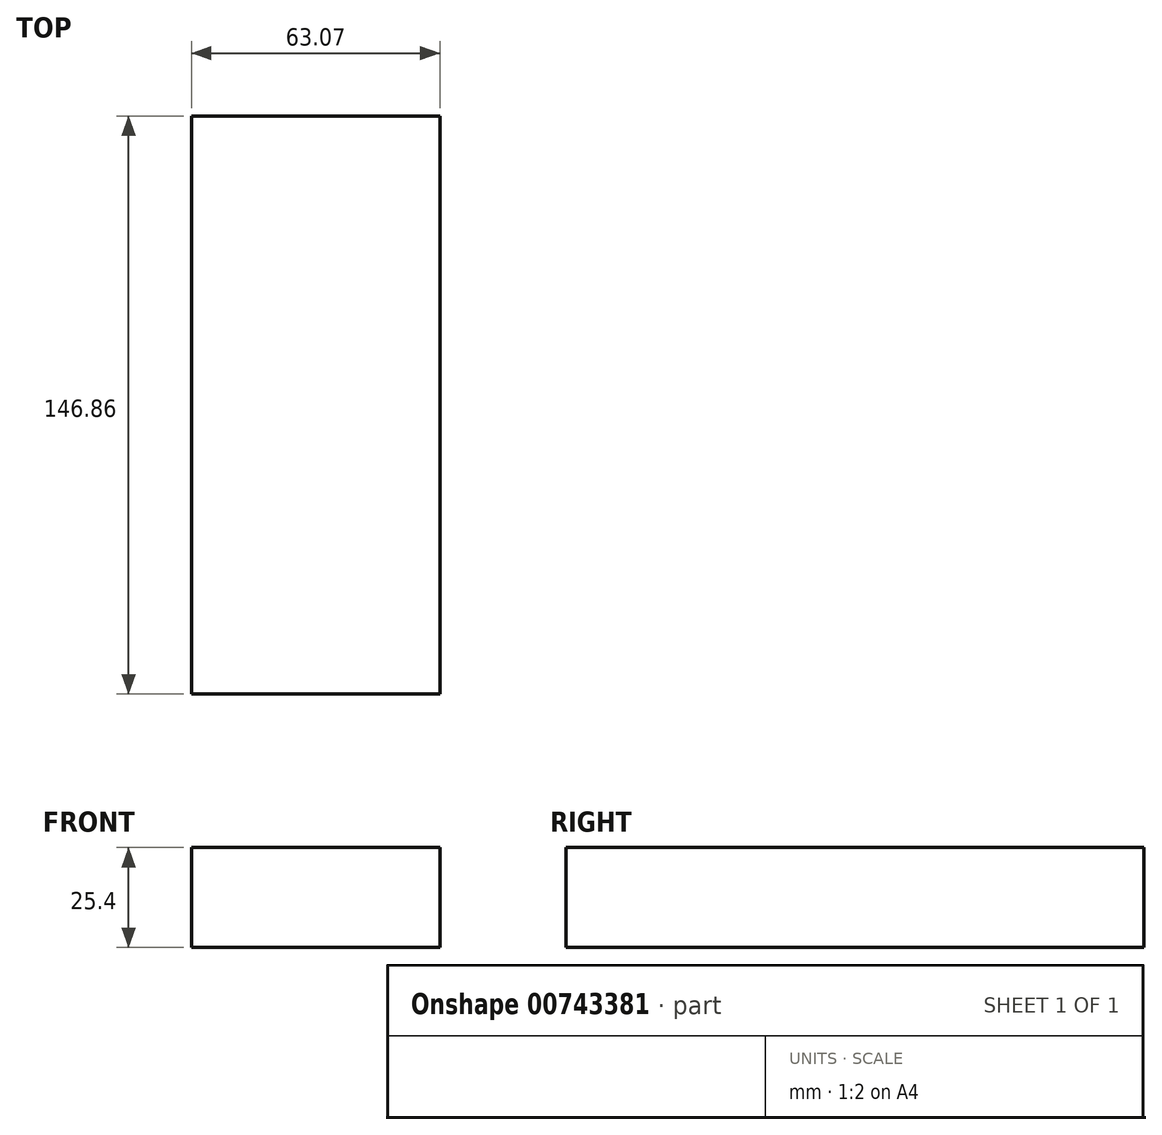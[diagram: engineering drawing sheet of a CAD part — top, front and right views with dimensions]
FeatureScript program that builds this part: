
annotation { "Feature Type Name" : "Feature", "Feature Type Description" : "" }
export const myFeature = defineFeature(function(context is Context, id is Id, definition is map)
    precondition{}
    {
        {
            var Q0;
            Q0=qCreatedBy(makeId("Top.planeOp"),FACE);
            var sketch = newSketch(context, id + "F0", { "sketchPlane" : qUnion([Q0])});
            skLineSegment(sketch, "E0.bottom", {"start": v(0, 0) * mm, "end": v(-63.07, 0) * mm});
            skLineSegment(sketch, "E0.top", {"start": v(0, 146.86) * mm, "end": v(-63.07, 146.86) * mm});
            skLineSegment(sketch, "E0.left", {"start": v(0, 0) * mm, "end": v(0, 146.86) * mm});
            skLineSegment(sketch, "E0.right", {"start": v(-63.07, 0) * mm, "end": v(-63.07, 146.86) * mm});
            skSolve(sketch);
        }
        {
            var Q0;
            Q0=makeQuery(id+"F0.imprint","IMPRINT",FACE,{"disambiguationData":[TD([[makeQuery(id+"F0.imprint","IMPRINT",EDGE,{"derivedFrom":sQuery(id+"F0.wireOp",EDGE,"E0.bottom")}),-1.0]])]});
            extrude(context, id + "F1", {"entities" : qUnion([Q0]), "depth" : 25.4 * mm, "offsetDistance" : 25.4 * mm});
        }
    });
